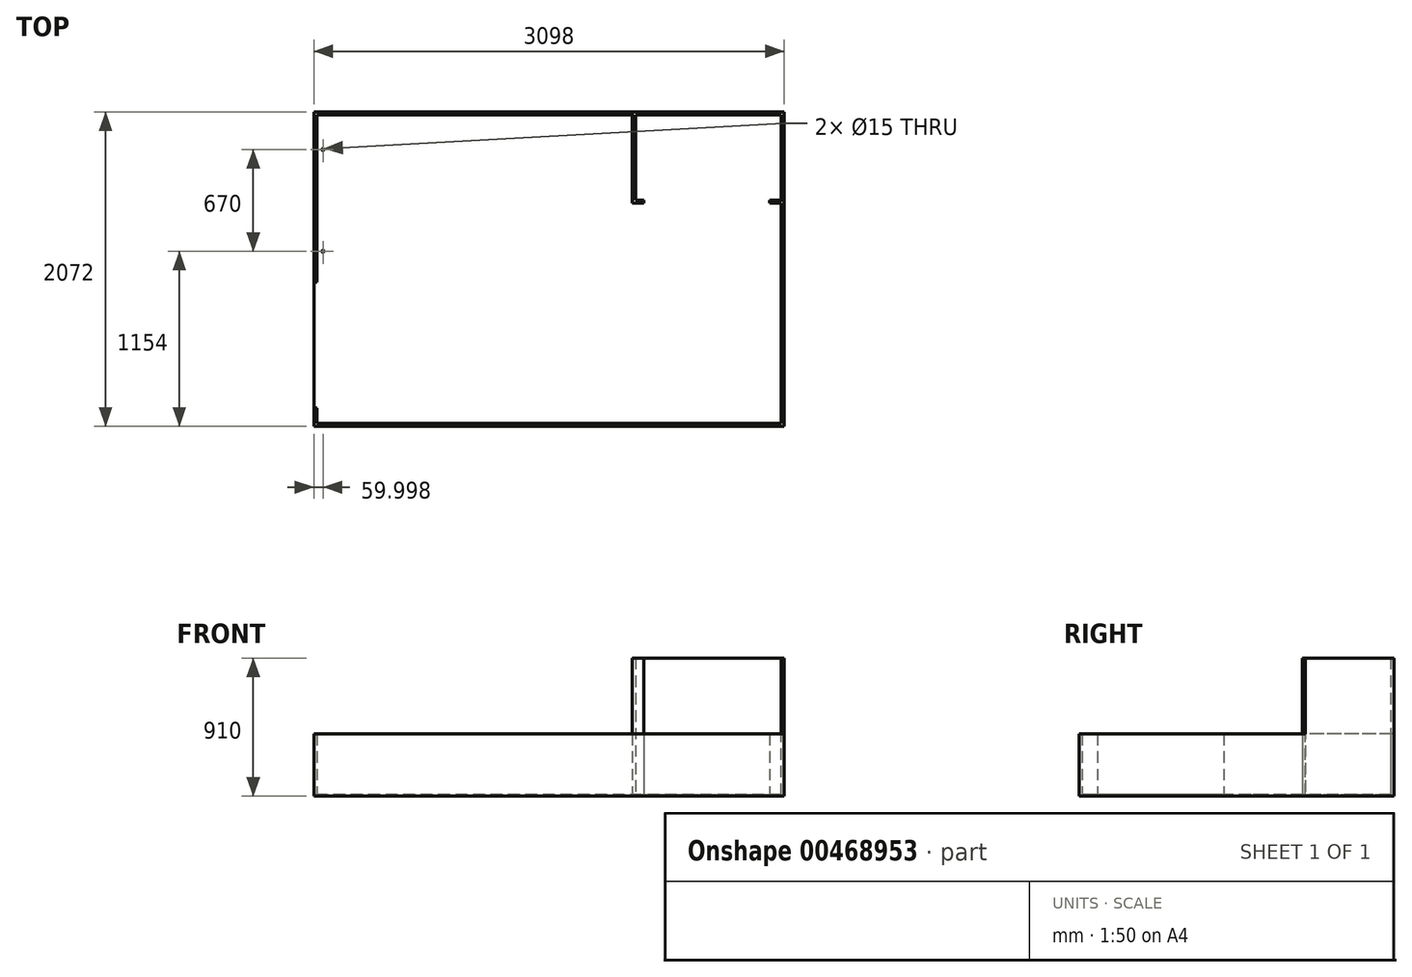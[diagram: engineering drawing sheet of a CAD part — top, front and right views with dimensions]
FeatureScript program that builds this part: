
annotation { "Feature Type Name" : "Feature", "Feature Type Description" : "" }
export const myFeature = defineFeature(function(context is Context, id is Id, definition is map)
    precondition{}
    {
        {
            var Q0;
            Q0=qCreatedBy(makeId("Top.planeOp"),FACE);
            var sketch = newSketch(context, id + "F0", { "sketchPlane" : qUnion([Q0])});
            skLineSegment(sketch, "E0", {"start": v(-1153.1, 305.24) * mm, "end": v(-1153.1, -1766.76) * mm});
            skLineSegment(sketch, "E1", {"start": v(-1153.1, 305.24) * mm, "end": v(964.9, 305.24) * mm});
            skLineSegment(sketch, "E2", {"start": v(964.9, -276.76) * mm, "end": v(964.9, 305.24) * mm});
            skLineSegment(sketch, "E3", {"start": v(964.9, -276.76) * mm, "end": v(1944.9, -276.76) * mm});
            skLineSegment(sketch, "E4", {"start": v(1944.9, -276.76) * mm, "end": v(1944.9, -1766.76) * mm});
            skLineSegment(sketch, "E5", {"start": v(1944.9, -1766.76) * mm, "end": v(-1153.1, -1766.76) * mm});
            skLineSegment(sketch, "E6.bottom", {"start": v(964.9, 305.24) * mm, "end": v(1944.9, 305.24) * mm});
            skLineSegment(sketch, "E6.left", {"start": v(964.9, 305.24) * mm, "end": v(964.9, -276.76) * mm});
            skLineSegment(sketch, "E6.right", {"start": v(1944.9, 305.24) * mm, "end": v(1944.9, -276.76) * mm});
            skSolve(sketch);
        }
        {
            var Q0;
            Q0 = qSketchRegion(id + "F0", true);
            extrude(context, id + "F1", {"entities" : qUnion([Q0]), "depth" : 10 * mm});
        }
        {
            var Q0;
            Q0=makeQuery(id+"F1.opExtrude","CAP_FACE",FACE,{"disambiguationData":[OSD([sQuery(id+"F0.wireOp",EDGE,"E0"),sQuery(id+"F0.wireOp",EDGE,"E1"),sQuery(id+"F0.wireOp",EDGE,"E2"),sQuery(id+"F0.wireOp",EDGE,"E3"),sQuery(id+"F0.wireOp",EDGE,"E4"),sQuery(id+"F0.wireOp",EDGE,"E5")])],"isStart":false});
            var sketch = newSketch(context, id + "F2", { "sketchPlane" : qUnion([Q0])});
            skLineSegment(sketch, "E7.top", {"start": v(-1153.1, -815.76) * mm, "end": v(-1133.1, -815.76) * mm});
            skLineSegment(sketch, "E7.left", {"start": v(-1153.1, 305.24) * mm, "end": v(-1153.1, -815.76) * mm});
            skLineSegment(sketch, "E7.right", {"start": v(-1133.1, 285.24) * mm, "end": v(-1133.1, -815.76) * mm});
            skLineSegment(sketch, "E8.bottom", {"start": v(-1153.1, 305.24) * mm, "end": v(964.9, 305.24) * mm});
            skLineSegment(sketch, "E8.top", {"start": v(-1133.1, 285.24) * mm, "end": v(944.9, 285.24) * mm});
            skLineSegment(sketch, "E9.left", {"start": v(964.9, 305.24) * mm, "end": v(964.9, -276.76) * mm});
            skLineSegment(sketch, "E9.right", {"start": v(944.9, 285.24) * mm, "end": v(944.9, -296.76) * mm});
            skLineSegment(sketch, "E10.bottom", {"start": v(964.9, -276.76) * mm, "end": v(1019.12, -276.76) * mm});
            skLineSegment(sketch, "E10.top", {"start": v(944.9, -296.76) * mm, "end": v(1019.12, -296.76) * mm});
            skLineSegment(sketch, "E11.right", {"start": v(1924.9, -296.76) * mm, "end": v(1924.9, -1746.76) * mm});
            skLineSegment(sketch, "E12.top", {"start": v(1924.9, -1746.76) * mm, "end": v(-1133.1, -1746.76) * mm});
            skLineSegment(sketch, "E13", {"start": v(1944.9, -276.76) * mm, "end": v(1944.9, -1766.76) * mm});
            skLineSegment(sketch, "E14", {"start": v(1944.9, -1766.76) * mm, "end": v(-1153.1, -1766.76) * mm});
            skLineSegment(sketch, "E15", {"start": v(-1153.1, -1766.76) * mm, "end": v(-1153.1, -1645.76) * mm});
            skLineSegment(sketch, "E16", {"start": v(-1153.1, -1645.76) * mm, "end": v(-1133.1, -1645.76) * mm});
            skLineSegment(sketch, "E17", {"start": v(-1133.1, -1645.76) * mm, "end": v(-1133.1, -1746.76) * mm});
            skLineSegment(sketch, "E18", {"start": v(1019.12, -276.76) * mm, "end": v(1019.12, -296.76) * mm});
            skLineSegment(sketch, "E19", {"start": v(1849.12, -276.76) * mm, "end": v(1849.12, -296.76) * mm});
            skLineSegment(sketch, "E20.trimOffspring", {"start": v(1849.12, -276.76) * mm, "end": v(1944.9, -276.76) * mm});
            skLineSegment(sketch, "E21.trimOffspring", {"start": v(1849.12, -296.76) * mm, "end": v(1924.9, -296.76) * mm});
            skSolve(sketch);
        }
        {
            var Q0;
            Q0=makeQuery(id+"F2.imprint","IMPRINT",FACE,{"disambiguationData":[TD([[makeQuery(id+"F2.imprint","IMPRINT",EDGE,{"derivedFrom":sQuery(id+"F2.wireOp",EDGE,"E7.top")}),1.0]])]});
            var Q1;
            Q1=makeQuery(id+"F2.imprint","IMPRINT",FACE,{"disambiguationData":[TD([[makeQuery(id+"F2.imprint","IMPRINT",EDGE,{"derivedFrom":sQuery(id+"F2.wireOp",EDGE,"E11.right")}),1.0]])]});
            extrude(context, id + "F3", {"entities" : qUnion([Q0, Q1]), "operationType" : NewBodyOperationType.ADD, "depth" : 400 * mm});
        }
        {
            var Q0;
            Q0=makeQuery(id+"F1.opExtrude","CAP_FACE",FACE,{"disambiguationData":[OSD([sQuery(id+"F0.wireOp",EDGE,"E0"),sQuery(id+"F0.wireOp",EDGE,"E1"),sQuery(id+"F0.wireOp",EDGE,"E2"),sQuery(id+"F0.wireOp",EDGE,"E3"),sQuery(id+"F0.wireOp",EDGE,"E4"),sQuery(id+"F0.wireOp",EDGE,"E5")])],"isStart":false});
            var sketch = newSketch(context, id + "F4", { "sketchPlane" : qUnion([Q0])});
            skCircle(sketch, "E22", {"center": v(-1093.1, 57.24) * mm, "radius": 7.5 * mm});
            skCircle(sketch, "E23", {"center": v(-1093.1, -612.76) * mm, "radius": 7.5 * mm});
            skSolve(sketch);
        }
        {
            var Q0;
            Q0 = qSketchRegion(id + "F4", true);
            extrude(context, id + "F5", {"entities" : qUnion([Q0]), "operationType" : NewBodyOperationType.REMOVE, "oppositeDirection" : true, "depth" : 25 * mm});
        }
        {
            var Q0;
            Q0=makeQuery(id+"F1.opExtrude","CAP_FACE",FACE,{"disambiguationData":[OSD([sQuery(id+"F0.wireOp",EDGE,"E0"),sQuery(id+"F0.wireOp",EDGE,"E1"),sQuery(id+"F0.wireOp",EDGE,"E4"),sQuery(id+"F0.wireOp",EDGE,"E5"),sQuery(id+"F0.wireOp",EDGE,"E6.bottom"),sQuery(id+"F0.wireOp",EDGE,"E6.right")])],"isStart":false});
            var sketch = newSketch(context, id + "F6", { "sketchPlane" : qUnion([Q0])});
            skLineSegment(sketch, "E24.bottom", {"start": v(1944.9, -276.76) * mm, "end": v(1924.9, -276.76) * mm});
            skLineSegment(sketch, "E24.left", {"start": v(1944.9, -276.76) * mm, "end": v(1944.9, 305.24) * mm});
            skLineSegment(sketch, "E24.right", {"start": v(1924.9, -276.76) * mm, "end": v(1924.9, 285.24) * mm});
            skLineSegment(sketch, "E25.bottom", {"start": v(964.9, 305.24) * mm, "end": v(1944.9, 305.24) * mm});
            skLineSegment(sketch, "E25.top", {"start": v(964.9, 285.24) * mm, "end": v(1924.9, 285.24) * mm});
            skPoint(sketch, "E24.top.end.orphan", {"position": v(1944.9, 305.24) * mm});
            skLineSegment(sketch, "E26", {"start": v(1019.12, -276.76) * mm, "end": v(1019.12, -296.76) * mm});
            skLineSegment(sketch, "E27", {"start": v(1019.12, -296.76) * mm, "end": v(944.9, -296.76) * mm});
            skLineSegment(sketch, "E28", {"start": v(944.9, -296.76) * mm, "end": v(944.9, 305.24) * mm});
            skLineSegment(sketch, "E29", {"start": v(944.9, 305.24) * mm, "end": v(964.9, 305.24) * mm});
            skLineSegment(sketch, "E30", {"start": v(964.9, -276.76) * mm, "end": v(1019.12, -276.76) * mm});
            skLineSegment(sketch, "E31", {"start": v(964.9, 285.24) * mm, "end": v(964.9, -276.76) * mm});
            skSolve(sketch);
        }
        {
            var Q0;
            Q0 = qSketchRegion(id + "F6", true);
            extrude(context, id + "F7", {"entities" : qUnion([Q0]), "operationType" : NewBodyOperationType.ADD, "depth" : 900 * mm});
        }
    });
